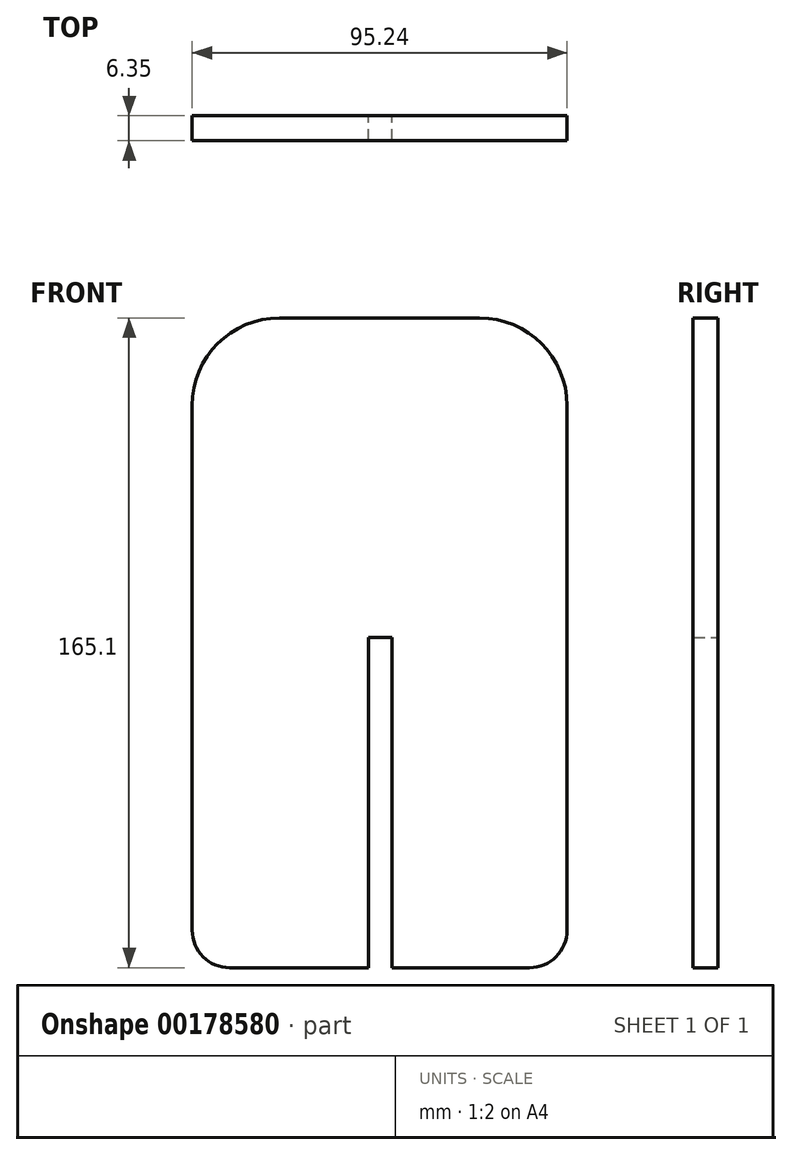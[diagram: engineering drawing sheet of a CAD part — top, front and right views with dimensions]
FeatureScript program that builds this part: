
annotation { "Feature Type Name" : "Feature", "Feature Type Description" : "" }
export const myFeature = defineFeature(function(context is Context, id is Id, definition is map)
    precondition{}
    {
        {
            var Q0;
            Q0=qCreatedBy(makeId("Front.planeOp"),FACE);
            var sketch = newSketch(context, id + "F0", { "sketchPlane" : qUnion([Q0])});
            skLineSegment(sketch, "E0.bottom", {"start": v(38.1, -82.55) * mm, "end": v(3.18, -82.55) * mm});
            skLineSegment(sketch, "E0.top", {"start": v(25.4, 82.55) * mm, "end": v(3.18, 82.55) * mm});
            skLineSegment(sketch, "E0.left", {"start": v(47.63, -73.03) * mm, "end": v(47.63, 60.33) * mm});
            skLineSegment(sketch, "E0.right", {"start": v(-47.63, -73.03) * mm, "end": v(-47.63, 60.33) * mm});
            skPoint(sketch, "E0.middle", {"position": v(0, 0) * mm});
            skPoint(sketch, "E1.visualSharp", {"position": v(-47.63, 82.55) * mm});
            skArc(sketch, "E1.filletArc", {"start": v(-25.4, 82.55) * mm, "mid": v(-41.12, 76.04) * mm, "end": v(-47.63, 60.33) * mm});
            skPoint(sketch, "E2.visualSharp", {"position": v(47.63, 82.55) * mm});
            skArc(sketch, "E2.filletArc", {"start": v(47.63, 60.33) * mm, "mid": v(41.12, 76.04) * mm, "end": v(25.4, 82.55) * mm});
            skPoint(sketch, "E3.visualSharp", {"position": v(-47.63, -82.55) * mm});
            skArc(sketch, "E3.filletArc", {"start": v(-47.63, -73.03) * mm, "mid": v(-44.84, -79.76) * mm, "end": v(-38.1, -82.55) * mm});
            skPoint(sketch, "E4.visualSharp", {"position": v(47.63, -82.55) * mm});
            skArc(sketch, "E4.filletArc", {"start": v(38.1, -82.55) * mm, "mid": v(44.84, -79.76) * mm, "end": v(47.63, -73.03) * mm});
            skLineSegment(sketch, "E5", {"start": v(0, 0) * mm, "end": v(0, 106.63) * mm, "construction": true});
            skLineSegment(sketch, "E6.0", {"start": v(3.18, -82.55) * mm, "end": v(3.18, 1.32) * mm});
            skLineSegment(sketch, "E7.0", {"start": v(-2.88, -82.55) * mm, "end": v(-2.88, 1.33) * mm});
            skLineSegment(sketch, "E8", {"start": v(-2.88, 1.33) * mm, "end": v(3.18, 1.32) * mm});
            skLineSegment(sketch, "E9.trimOffspring", {"start": v(-2.88, 82.55) * mm, "end": v(-25.4, 82.55) * mm});
            skLineSegment(sketch, "E10", {"start": v(-2.88, 82.55) * mm, "end": v(3.18, 82.55) * mm});
            skLineSegment(sketch, "E11.trimOffspring", {"start": v(-2.88, -82.55) * mm, "end": v(-38.1, -82.55) * mm});
            skSolve(sketch);
        }
        {
            var Q0;
            Q0 = qSketchRegion(id + "F0", true);
            extrude(context, id + "F1", {"entities" : qUnion([Q0]), "depth" : 6.35 * mm});
        }
    });
